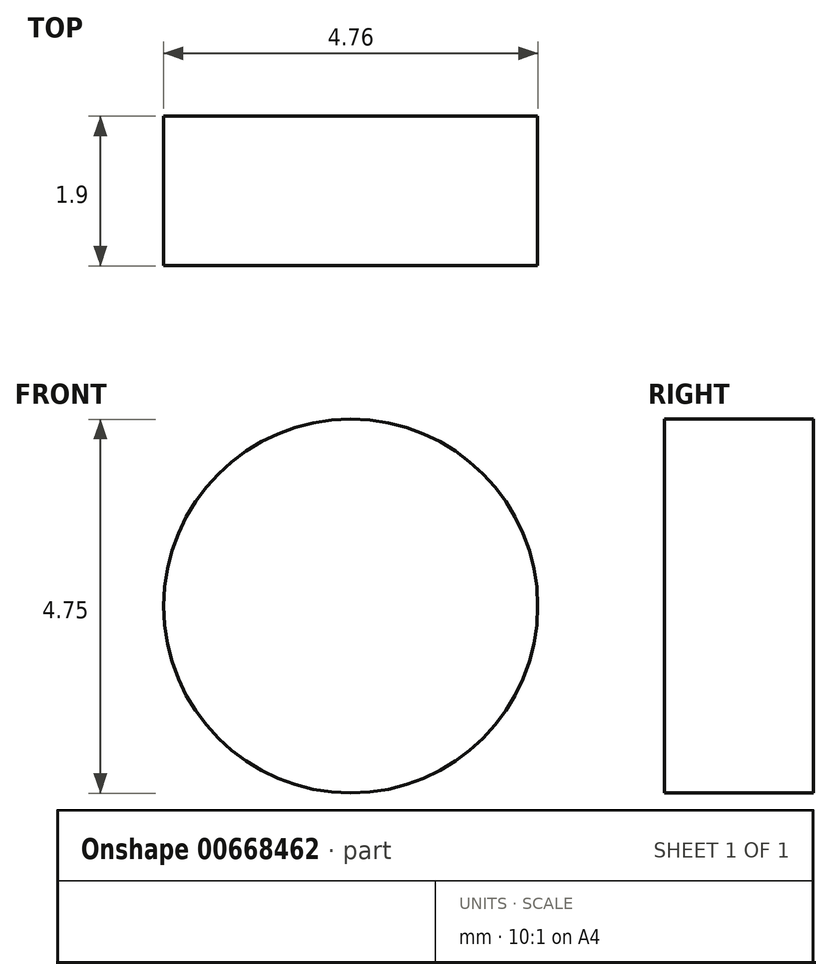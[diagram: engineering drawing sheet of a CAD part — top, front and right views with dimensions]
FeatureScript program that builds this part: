
annotation { "Feature Type Name" : "Feature", "Feature Type Description" : "" }
export const myFeature = defineFeature(function(context is Context, id is Id, definition is map)
    precondition{}
    {
        {
            var Q0;
            Q0=qCreatedBy(makeId("Front.planeOp"),FACE);
            var sketch = newSketch(context, id + "F0", { "sketchPlane" : qUnion([Q0])});
            skCircle(sketch, "E0.MirrorC", {"center": v(-4.12, 22.47) * mm, "radius": 2.38 * mm});
            skCircle(sketch, "E1.MirrorC", {"center": v(-4.12, 15.33) * mm, "radius": 1.6 * mm});
            skLineSegment(sketch, "E2", {"start": v(-7.3, 27.38) * mm, "end": v(-7.3, 15.33) * mm});
            skLineSegment(sketch, "E3", {"start": v(-4.12, 12.15) * mm, "end": v(0.67, 12.15) * mm});
            skPoint(sketch, "E4.center.orphan", {"position": v(27.63, 24.74) * mm});
            skPoint(sketch, "E5.visualSharp", {"position": v(-7.3, 12.15) * mm});
            skArc(sketch, "E5.filletArc", {"start": v(-7.3, 15.33) * mm, "mid": v(-6.37, 13.08) * mm, "end": v(-4.12, 12.15) * mm});
            skPoint(sketch, "E6.visualSharp", {"position": v(3.63, 12.15) * mm});
            skLineSegment(sketch, "E7.MirrorCS", {"start": v(27.63, 12.15) * mm, "end": v(22.84, 12.15) * mm});
            skArc(sketch, "E8.MirrorCS", {"start": v(30.8, 15.33) * mm, "mid": v(29.88, 13.08) * mm, "end": v(27.63, 12.15) * mm});
            skCircle(sketch, "E9.MirrorC", {"center": v(27.63, 15.33) * mm, "radius": 1.6 * mm});
            skCircle(sketch, "E10.MirrorC", {"center": v(27.63, 22.47) * mm, "radius": 2.38 * mm});
            skLineSegment(sketch, "E11", {"start": v(30.8, 27.38) * mm, "end": v(30.8, 15.33) * mm});
            skLineSegment(sketch, "E12", {"start": v(-7.3, 27.38) * mm, "end": v(30.8, 27.38) * mm});
            skPoint(sketch, "E13.end.orphan", {"position": v(0, -8.22) * mm});
            skLineSegment(sketch, "E14", {"start": v(0.67, 12.15) * mm, "end": v(22.84, 12.15) * mm});
            skSolve(sketch);
        }
        {
            var Q0;
            Q0=makeQuery(id+"F0.imprint","IMPRINT",FACE,{"disambiguationData":[TD([[makeQuery(id+"F0.imprint","IMPRINT",EDGE,{"derivedFrom":sQuery(id+"F0.wireOp",EDGE,"E0.MirrorC")}),1.0]])]});
            extrude(context, id + "F1", {"entities" : qUnion([Q0]), "depth" : 1.9 * mm});
        }
    });
